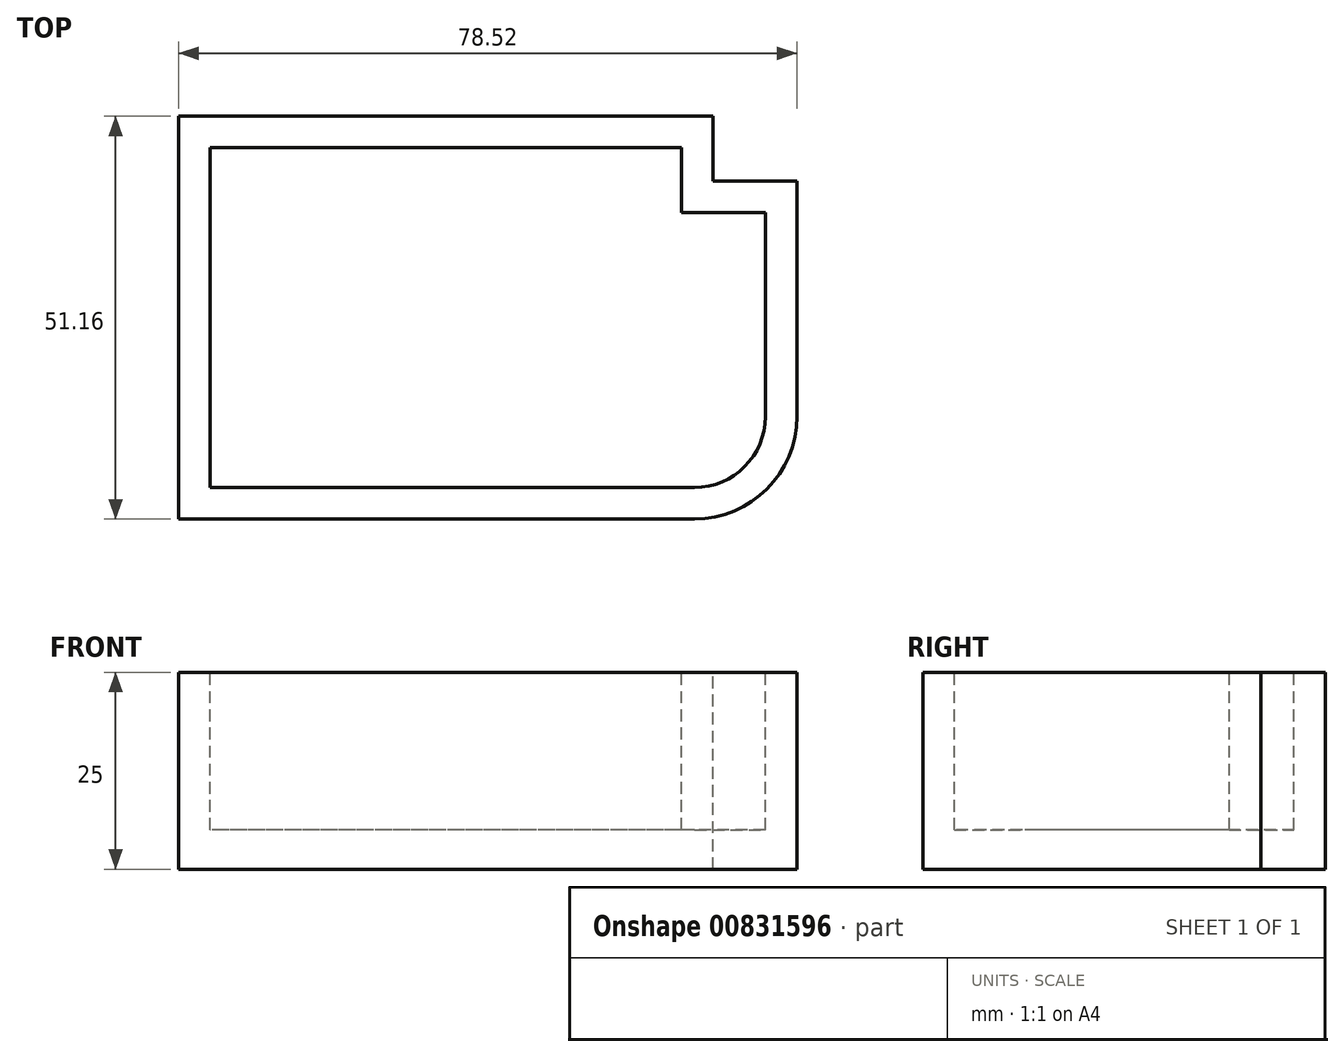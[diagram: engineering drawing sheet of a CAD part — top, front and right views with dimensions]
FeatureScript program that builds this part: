
annotation { "Feature Type Name" : "Feature", "Feature Type Description" : "" }
export const myFeature = defineFeature(function(context is Context, id is Id, definition is map)
    precondition{}
    {
        {
            var Q0;
            Q0=qCreatedBy(makeId("Top.planeOp"),FACE);
            var sketch = newSketch(context, id + "F0", { "sketchPlane" : qUnion([Q0])});
            skLineSegment(sketch, "E0.bottom", {"start": v(25.62, 22.58) * mm, "end": v(-36.26, 22.58) * mm, "construction": true});
            skLineSegment(sketch, "E0.top", {"start": v(26.26, -22.58) * mm, "end": v(-36.26, -22.58) * mm, "construction": true});
            skLineSegment(sketch, "E0.left", {"start": v(36.26, 14.35) * mm, "end": v(36.26, -12.58) * mm, "construction": true});
            skLineSegment(sketch, "E0.right", {"start": v(-36.26, 22.58) * mm, "end": v(-36.26, -22.58) * mm, "construction": true});
            skPoint(sketch, "E0.middle", {"position": v(0, 0) * mm});
            skPoint(sketch, "E1.visualSharp", {"position": v(36.26, -22.58) * mm});
            skArc(sketch, "E1.filletArc", {"start": v(26.26, -22.58) * mm, "mid": v(33.33, -19.65) * mm, "end": v(36.26, -12.58) * mm, "construction": true});
            skLineSegment(sketch, "E2", {"start": v(36.26, 14.35) * mm, "end": v(25.62, 14.35) * mm, "construction": true});
            skLineSegment(sketch, "E3", {"start": v(25.62, 14.35) * mm, "end": v(25.62, 22.58) * mm, "construction": true});
            skLineSegment(sketch, "E4.0", {"start": v(26.26, -25.58) * mm, "end": v(-39.26, -25.58) * mm});
            skLineSegment(sketch, "E4.1", {"start": v(-39.26, 25.58) * mm, "end": v(-39.26, -25.58) * mm});
            skLineSegment(sketch, "E4.2", {"start": v(39.26, 17.35) * mm, "end": v(39.26, -12.58) * mm});
            skLineSegment(sketch, "E4.3", {"start": v(39.26, 17.35) * mm, "end": v(28.62, 17.35) * mm});
            skLineSegment(sketch, "E4.4", {"start": v(28.62, 17.35) * mm, "end": v(28.62, 25.58) * mm});
            skArc(sketch, "E4.5", {"start": v(26.26, -25.58) * mm, "mid": v(35.45, -21.77) * mm, "end": v(39.26, -12.58) * mm});
            skLineSegment(sketch, "E4.6", {"start": v(28.62, 25.58) * mm, "end": v(-39.26, 25.58) * mm});
            skLineSegment(sketch, "E5.0", {"start": v(24.62, 13.35) * mm, "end": v(24.62, 21.58) * mm});
            skLineSegment(sketch, "E5.1", {"start": v(35.26, 13.35) * mm, "end": v(24.62, 13.35) * mm});
            skLineSegment(sketch, "E5.2", {"start": v(-35.26, 21.58) * mm, "end": v(-35.26, -21.58) * mm});
            skLineSegment(sketch, "E5.3", {"start": v(26.26, -21.58) * mm, "end": v(-35.26, -21.58) * mm});
            skArc(sketch, "E5.4", {"start": v(26.26, -21.58) * mm, "mid": v(32.63, -18.94) * mm, "end": v(35.26, -12.58) * mm});
            skLineSegment(sketch, "E5.5", {"start": v(24.62, 21.58) * mm, "end": v(-35.26, 21.58) * mm});
            skLineSegment(sketch, "E5.6", {"start": v(35.26, 13.35) * mm, "end": v(35.26, -12.58) * mm});
            skSolve(sketch);
        }
        {
            var Q0;
            Q0=makeQuery(id+"F0.imprint","IMPRINT",FACE,{"disambiguationData":[TD([[makeQuery(id+"F0.imprint","IMPRINT",EDGE,{"derivedFrom":sQuery(id+"F0.wireOp",EDGE,"E4.0")}),-1.0]])]});
            var Q1;
            Q1=makeQuery(id+"F0.imprint","IMPRINT",FACE,{"disambiguationData":[TD([[makeQuery(id+"F0.imprint","IMPRINT",EDGE,{"derivedFrom":sQuery(id+"F0.wireOp",EDGE,"E5.0")}),1.0]])]});
            extrude(context, id + "F1", {"entities" : qUnion([Q0, Q1]), "oppositeDirection" : true, "depth" : 25 * mm, "offsetDistance" : 25 * mm});
        }
        {
            var Q0;
            Q0=makeQuery(id+"F0.imprint","IMPRINT",FACE,{"disambiguationData":[TD([[makeQuery(id+"F0.imprint","IMPRINT",EDGE,{"derivedFrom":sQuery(id+"F0.wireOp",EDGE,"E5.0")}),1.0]])]});
            extrude(context, id + "F2", {"entities" : qUnion([Q0]), "operationType" : NewBodyOperationType.REMOVE, "oppositeDirection" : true, "depth" : 20 * mm, "offsetDistance" : 25 * mm});
        }
    });
